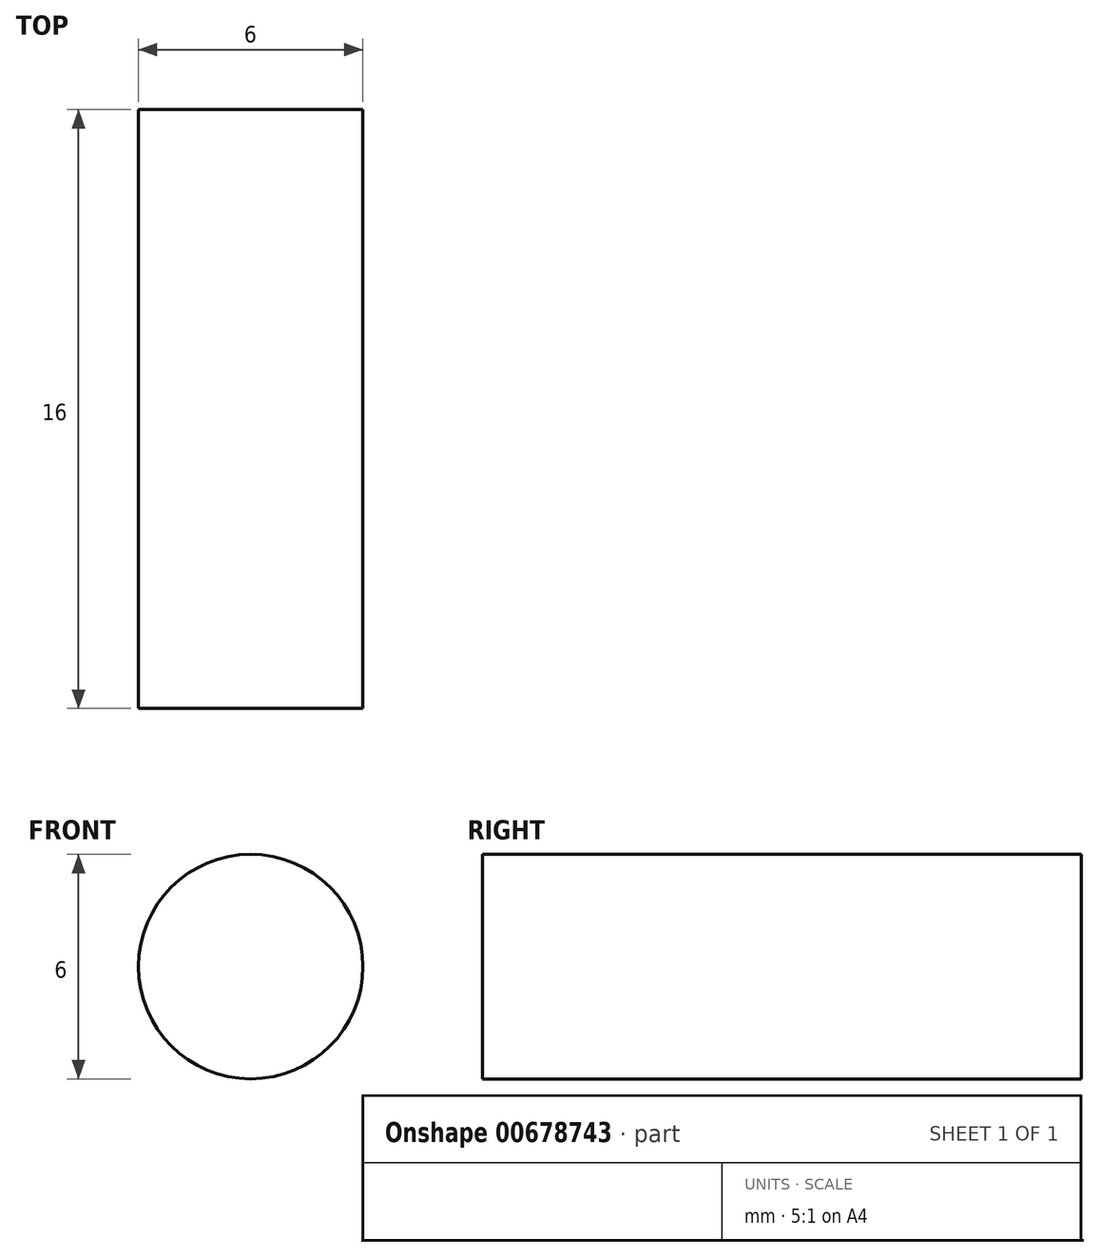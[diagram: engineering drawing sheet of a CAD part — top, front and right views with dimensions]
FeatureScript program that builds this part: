
annotation { "Feature Type Name" : "Feature", "Feature Type Description" : "" }
export const myFeature = defineFeature(function(context is Context, id is Id, definition is map)
    precondition{}
    {
        {
            var Q0;
            Q0=qCreatedBy(makeId("Front.planeOp"),FACE);
            var sketch = newSketch(context, id + "F0", { "sketchPlane" : qUnion([Q0])});
            skCircle(sketch, "E0", {"center": v(0, 0) * mm, "radius": 3 * mm});
            skSolve(sketch);
        }
        {
            var Q0;
            Q0=makeQuery(id+"F0.imprint","IMPRINT",FACE,{"disambiguationData":[TD([[makeQuery(id+"F0.imprint","IMPRINT",EDGE,{"derivedFrom":sQuery(id+"F0.wireOp",EDGE,"E0")}),1.0]])]});
            extrude(context, id + "F1", {"entities" : qUnion([Q0]), "depth" : 16 * mm, "offsetDistance" : 25 * mm});
        }
    });
